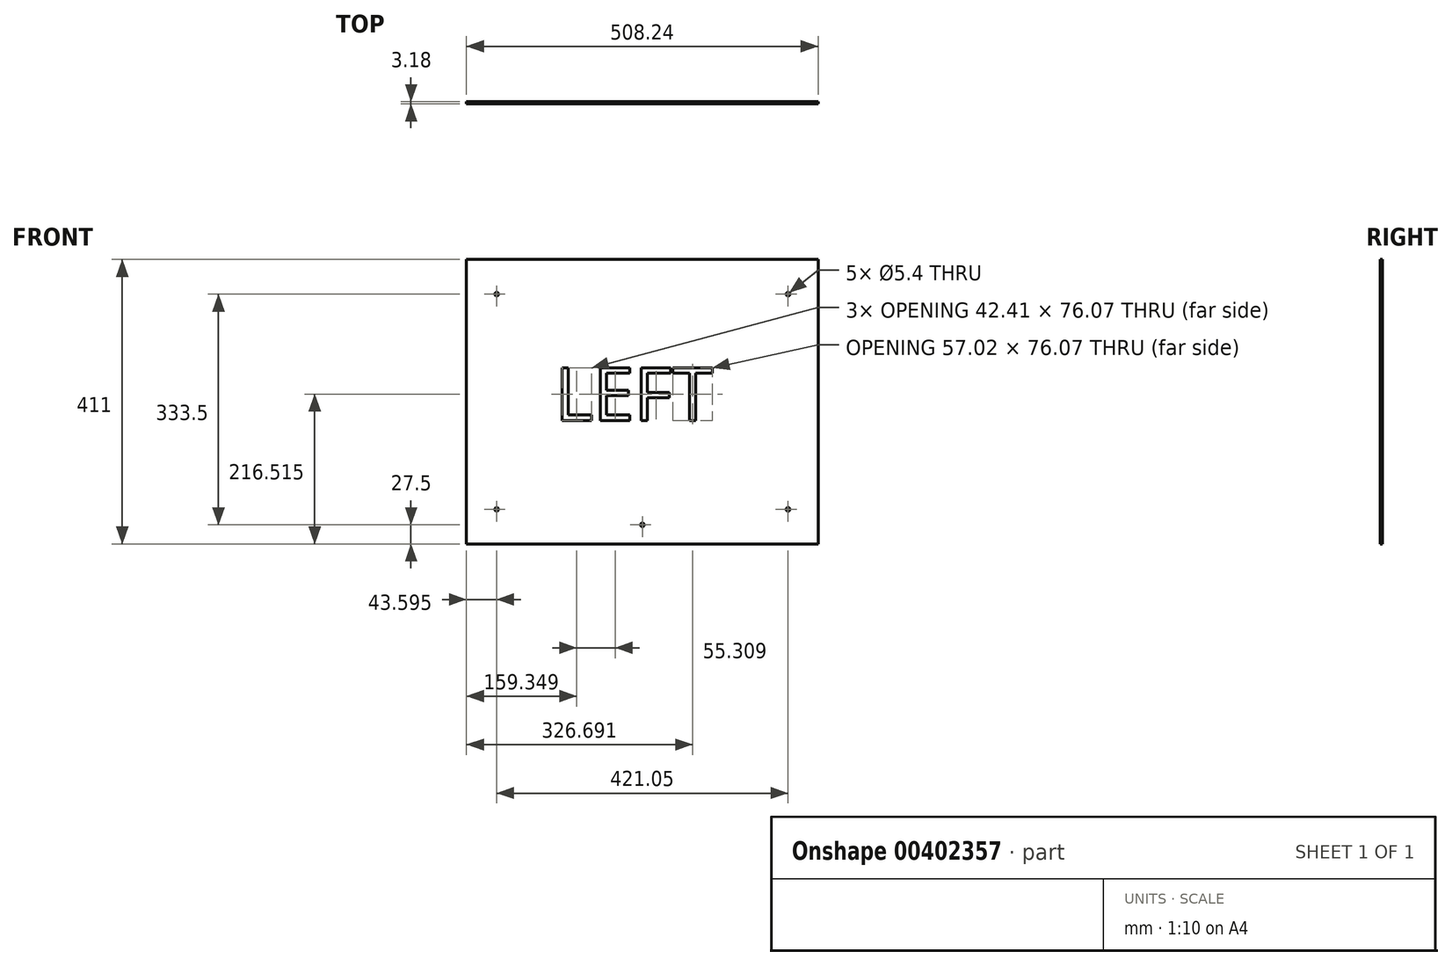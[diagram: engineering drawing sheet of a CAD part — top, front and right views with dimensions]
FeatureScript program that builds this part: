
annotation { "Feature Type Name" : "Feature", "Feature Type Description" : "" }
export const myFeature = defineFeature(function(context is Context, id is Id, definition is map)
    precondition{}
    {
        {
            var Q0;
            Q0=qCreatedBy(makeId("Front.planeOp"),FACE);
            var sketch = newSketch(context, id + "F0", { "sketchPlane" : qUnion([Q0])});
            skLineSegment(sketch, "E0.bottom", {"start": v(-254.12, 205.5) * mm, "end": v(254.12, 205.5) * mm});
            skLineSegment(sketch, "E0.top", {"start": v(-254.13, -205.5) * mm, "end": v(254.12, -205.5) * mm});
            skLineSegment(sketch, "E0.left", {"start": v(-254.12, 205.5) * mm, "end": v(-254.13, -205.5) * mm});
            skLineSegment(sketch, "E0.right", {"start": v(254.12, 205.5) * mm, "end": v(254.12, -205.5) * mm});
            skPoint(sketch, "E0.middle", {"position": v(0, 0) * mm});
            skSolve(sketch);
        }
        {
            var Q0;
            Q0=makeQuery(id+"F0.imprint","IMPRINT",FACE,{"disambiguationData":[TD([[makeQuery(id+"F0.imprint","IMPRINT",EDGE,{"derivedFrom":sQuery(id+"F0.wireOp",EDGE,"E0.bottom")}),-1.0]])]});
            extrude(context, id + "F1", {"entities" : qUnion([Q0]), "depth" : (.125 * 25.4) * mm});
        }
        {
            var Q0;
            Q0=makeQuery(id+"FpBMKNsvPauGnLh_1.boolean.opBoolean","MERGE",FACE,{"derivedFrom":[makeQuery(id+"F1.opExtrude","CAP_FACE",FACE,{"disambiguationData":[OSD([sQuery(id+"F0.wireOp",EDGE,"E0.bottom"),sQuery(id+"F0.wireOp",EDGE,"E0.top"),sQuery(id+"F0.wireOp",EDGE,"E0.left"),sQuery(id+"F0.wireOp",EDGE,"E0.right")])],"isStart":false}),makeQuery(id+"FpBMKNsvPauGnLh_1.opExtrude","CAP_FACE",FACE,{"disambiguationData":[OSD([sQuery(id+"FzWSCRHqbb1aw3Q_1.wireOp",EDGE,"pNUi7Ymo-PIhC-6L1w-etEG-QhCEAS8cRYcq.bottom"),sQuery(id+"FzWSCRHqbb1aw3Q_1.wireOp",EDGE,"pNUi7Ymo-PIhC-6L1w-etEG-QhCEAS8cRYcq.top"),sQuery(id+"FzWSCRHqbb1aw3Q_1.wireOp",EDGE,"pNUi7Ymo-PIhC-6L1w-etEG-QhCEAS8cRYcq.left"),sQuery(id+"FzWSCRHqbb1aw3Q_1.wireOp",EDGE,"pNUi7Ymo-PIhC-6L1w-etEG-QhCEAS8cRYcq.right")])],"isStart":true}),makeQuery(id+"FpBMKNsvPauGnLh_1.opExtrude","CAP_FACE",FACE,{"disambiguationData":[OSD([sQuery(id+"FzWSCRHqbb1aw3Q_1.wireOp",EDGE,"rslhBf2L-x2pj-VNBq-4pd2-VHaR9mQvUz9W.bottom"),sQuery(id+"FzWSCRHqbb1aw3Q_1.wireOp",EDGE,"rslhBf2L-x2pj-VNBq-4pd2-VHaR9mQvUz9W.top"),sQuery(id+"FzWSCRHqbb1aw3Q_1.wireOp",EDGE,"rslhBf2L-x2pj-VNBq-4pd2-VHaR9mQvUz9W.left"),sQuery(id+"FzWSCRHqbb1aw3Q_1.wireOp",EDGE,"rslhBf2L-x2pj-VNBq-4pd2-VHaR9mQvUz9W.right")])],"isStart":true})]});
            var sketch = newSketch(context, id + "F2", { "sketchPlane" : qUnion([Q0])});
            skText(sketch, "E1", { "text": "LEFT", "fontName": "OpenSans-Regular.ttf"});
            const initialGuessF2  = {"E1": [-0.12643, -0.02702, 1, 0, 0.07672]};
            skSetInitialGuess(sketch, initialGuessF2);
            skSolve(sketch);
        }
        {
            var Q0;
            Q0=makeQuery(id+"F2.imprint","IMPRINT",FACE,{"disambiguationData":[TD([[makeQuery(id+"F2.imprint","IMPRINT",EDGE,{"derivedFrom":sQuery(id+"F2.wireOp",EDGE,"E1.sketch_text.stroke-0")}),-1.0]])]});
            var Q1;
            Q1=makeQuery(id+"F2.imprint","IMPRINT",FACE,{"disambiguationData":[TD([[makeQuery(id+"F2.imprint","IMPRINT",EDGE,{"derivedFrom":sQuery(id+"F2.wireOp",EDGE,"E1.sketch_text.stroke-6")}),-1.0]])]});
            var Q2;
            Q2=makeQuery(id+"F2.imprint","IMPRINT",FACE,{"disambiguationData":[TD([[makeQuery(id+"F2.imprint","IMPRINT",EDGE,{"derivedFrom":sQuery(id+"F2.wireOp",EDGE,"E1.sketch_text.stroke-18")}),-1.0]])]});
            var Q3;
            Q3=makeQuery(id+"F2.imprint","IMPRINT",FACE,{"disambiguationData":[TD([[makeQuery(id+"F2.imprint","IMPRINT",EDGE,{"derivedFrom":sQuery(id+"F2.wireOp",EDGE,"E1.sketch_text.stroke-28")}),-1.0]])]});
            extrude(context, id + "F3", {"entities" : qUnion([Q0, Q1, Q2, Q3]), "operationType" : NewBodyOperationType.REMOVE, "oppositeDirection" : true, "depth" : 25 * mm});
        }
        {
            var Q0;
            Q0=makeQuery(id+"FpBMKNsvPauGnLh_1.boolean.opBoolean","MERGE",FACE,{"derivedFrom":[makeQuery(id+"F1.opExtrude","CAP_FACE",FACE,{"disambiguationData":[OSD([sQuery(id+"F0.wireOp",EDGE,"E0.bottom"),sQuery(id+"F0.wireOp",EDGE,"E0.top"),sQuery(id+"F0.wireOp",EDGE,"E0.left"),sQuery(id+"F0.wireOp",EDGE,"E0.right")])],"isStart":false}),makeQuery(id+"FpBMKNsvPauGnLh_1.opExtrude","CAP_FACE",FACE,{"disambiguationData":[OSD([sQuery(id+"FzWSCRHqbb1aw3Q_1.wireOp",EDGE,"pNUi7Ymo-PIhC-6L1w-etEG-QhCEAS8cRYcq.bottom"),sQuery(id+"FzWSCRHqbb1aw3Q_1.wireOp",EDGE,"pNUi7Ymo-PIhC-6L1w-etEG-QhCEAS8cRYcq.top"),sQuery(id+"FzWSCRHqbb1aw3Q_1.wireOp",EDGE,"pNUi7Ymo-PIhC-6L1w-etEG-QhCEAS8cRYcq.left"),sQuery(id+"FzWSCRHqbb1aw3Q_1.wireOp",EDGE,"pNUi7Ymo-PIhC-6L1w-etEG-QhCEAS8cRYcq.right")])],"isStart":true}),makeQuery(id+"FpBMKNsvPauGnLh_1.opExtrude","CAP_FACE",FACE,{"disambiguationData":[OSD([sQuery(id+"FzWSCRHqbb1aw3Q_1.wireOp",EDGE,"rslhBf2L-x2pj-VNBq-4pd2-VHaR9mQvUz9W.bottom"),sQuery(id+"FzWSCRHqbb1aw3Q_1.wireOp",EDGE,"rslhBf2L-x2pj-VNBq-4pd2-VHaR9mQvUz9W.top"),sQuery(id+"FzWSCRHqbb1aw3Q_1.wireOp",EDGE,"rslhBf2L-x2pj-VNBq-4pd2-VHaR9mQvUz9W.left"),sQuery(id+"FzWSCRHqbb1aw3Q_1.wireOp",EDGE,"rslhBf2L-x2pj-VNBq-4pd2-VHaR9mQvUz9W.right")])],"isStart":true})]});
            var sketch = newSketch(context, id + "F4", { "sketchPlane" : qUnion([Q0])});
            skCircle(sketch, "E2", {"center": v(-210.52, 155.5) * mm, "radius": 2.7 * mm});
            skCircle(sketch, "E3", {"center": v(-210.52, -155.5) * mm, "radius": 2.7 * mm});
            skCircle(sketch, "E4", {"center": v(210.53, 155.5) * mm, "radius": 2.7 * mm});
            skCircle(sketch, "E5", {"center": v(210.53, -155.5) * mm, "radius": 2.7 * mm});
            skCircle(sketch, "E6", {"center": v(-0.03, -178) * mm, "radius": 2.7 * mm});
            skLineSegment(sketch, "E7.0.0", {"start": v(-254.13, -205.5) * mm, "end": v(254.12, -205.5) * mm, "construction": true});
            skLineSegment(sketch, "E7.0.2", {"start": v(254.12, -205.5) * mm, "end": v(-254.13, -205.5) * mm, "construction": true});
            skLineSegment(sketch, "E8.0", {"start": v(-254.12, 205.5) * mm, "end": v(-254.13, -205.5) * mm, "construction": true});
            skLineSegment(sketch, "E9.0", {"start": v(254.12, 205.5) * mm, "end": v(254.12, -205.5) * mm, "construction": true});
            skLineSegment(sketch, "E10.0.0", {"start": v(254.12, 205.5) * mm, "end": v(-254.12, 205.5) * mm, "construction": true});
            skLineSegment(sketch, "E10.0.2", {"start": v(-254.12, 205.5) * mm, "end": v(254.12, 205.5) * mm, "construction": true});
            skSolve(sketch);
        }
        {
            var Q0;
            Q0 = qSketchRegion(id + "F4", true);
            extrude(context, id + "F5", {"entities" : qUnion([Q0]), "operationType" : NewBodyOperationType.REMOVE, "oppositeDirection" : true, "depth" : 25 * mm});
        }
    });
